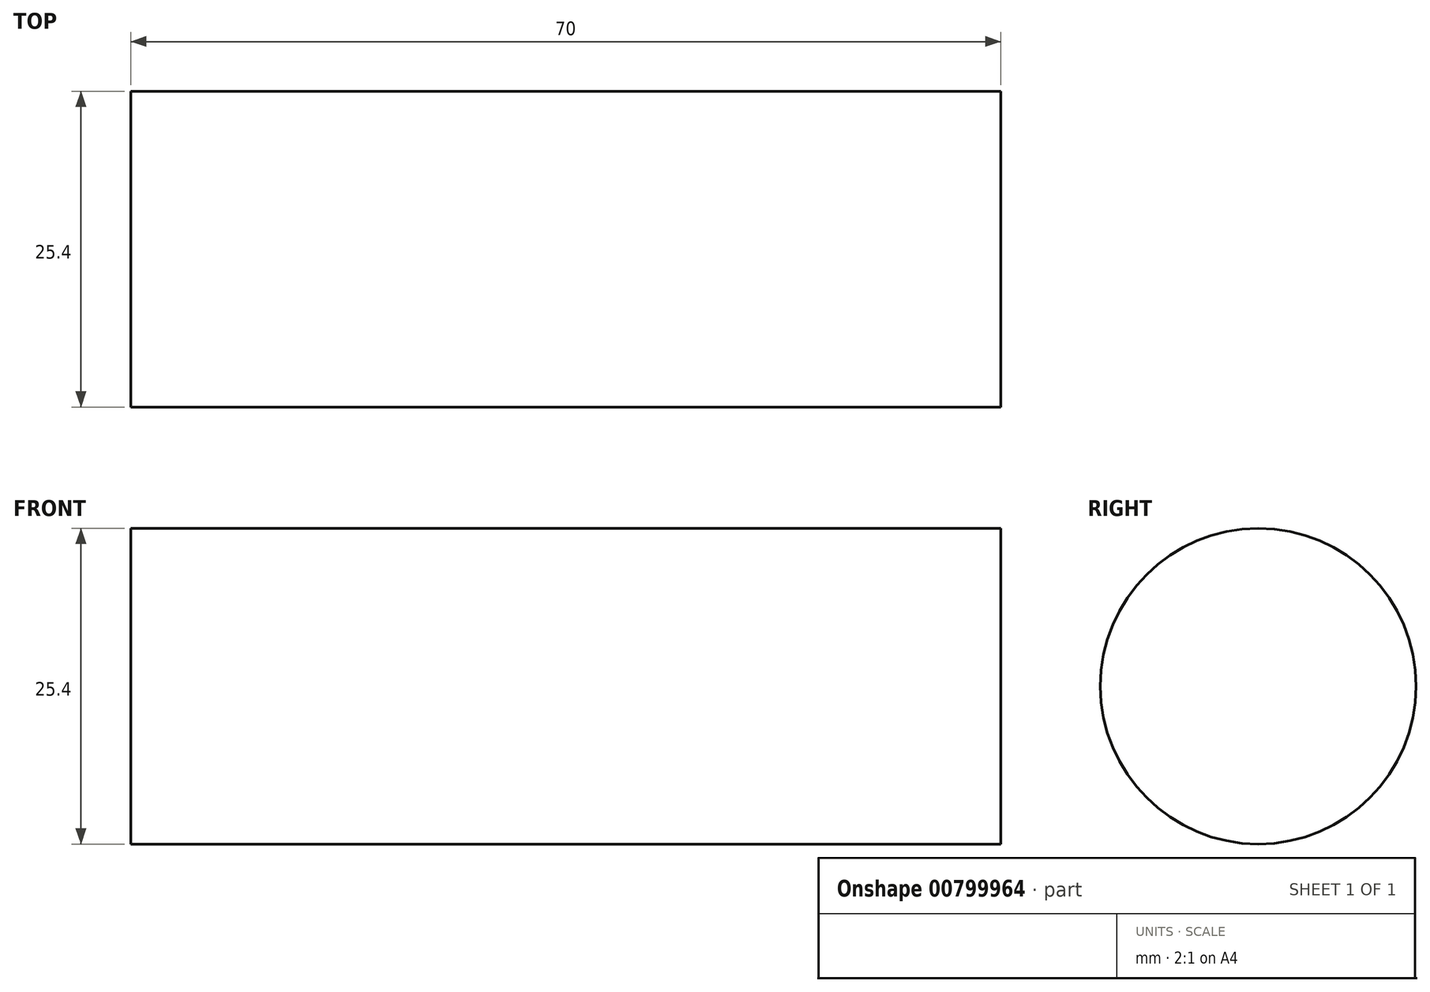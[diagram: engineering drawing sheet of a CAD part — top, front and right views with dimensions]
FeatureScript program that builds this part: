
annotation { "Feature Type Name" : "Feature", "Feature Type Description" : "" }
export const myFeature = defineFeature(function(context is Context, id is Id, definition is map)
    precondition{}
    {
        {
            var Q0;
            Q0=qCreatedBy(makeId("Right.planeOp"),FACE);
            var sketch = newSketch(context, id + "F0", { "sketchPlane" : qUnion([Q0])});
            skCircle(sketch, "E0", {"center": v(0, 0) * mm, "radius": 12.7 * mm});
            skSolve(sketch);
        }
        {
            var Q0;
            Q0 = qSketchRegion(id + "F0", true);
            extrude(context, id + "F1", {"entities" : qUnion([Q0]), "depth" : 70 * mm, "offsetDistance" : 25 * mm});
        }
    });
